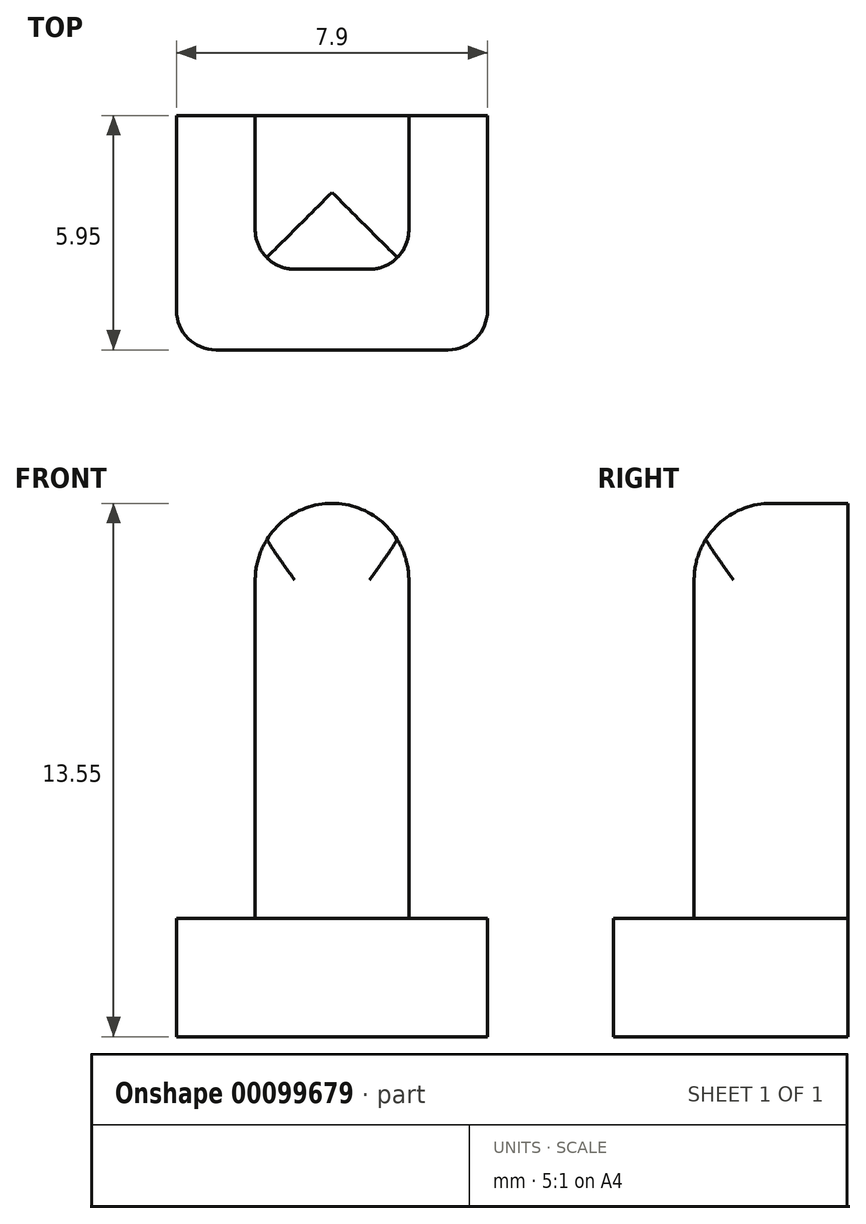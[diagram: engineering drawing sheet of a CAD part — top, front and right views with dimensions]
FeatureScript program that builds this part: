
annotation { "Feature Type Name" : "Feature", "Feature Type Description" : "" }
export const myFeature = defineFeature(function(context is Context, id is Id, definition is map)
    precondition{}
    {
        {
            var Q0;
            Q0=qCreatedBy(makeId("Top.planeOp"),FACE);
            var sketch = newSketch(context, id + "F0", { "sketchPlane" : qUnion([Q0])});
            skLineSegment(sketch, "E0.bottom", {"start": v(-3.95, 0) * mm, "end": v(3.95, 0) * mm});
            skLineSegment(sketch, "E0.top", {"start": v(-3.95, -5.95) * mm, "end": v(3.95, -5.95) * mm});
            skLineSegment(sketch, "E0.left", {"start": v(-3.95, 0) * mm, "end": v(-3.95, -5.95) * mm});
            skLineSegment(sketch, "E0.right", {"start": v(3.95, 0) * mm, "end": v(3.95, -5.95) * mm});
            skSolve(sketch);
        }
        {
            var Q0;
            Q0=makeQuery(id+"F0.imprint","IMPRINT",FACE,{"disambiguationData":[TD([[makeQuery(id+"F0.imprint","IMPRINT",EDGE,{"derivedFrom":sQuery(id+"F0.wireOp",EDGE,"E0.bottom")}),-1.0]])]});
            extrude(context, id + "F1", {"entities" : qUnion([Q0]), "depth" : 3 * mm});
        }
        {
            var Q0;
            Q0=makeQuery(id+"F1.opExtrude","CAP_FACE",FACE,{"disambiguationData":[OSD([sQuery(id+"F0.wireOp",EDGE,"E0.bottom"),sQuery(id+"F0.wireOp",EDGE,"E0.top"),sQuery(id+"F0.wireOp",EDGE,"E0.left"),sQuery(id+"F0.wireOp",EDGE,"E0.right")])],"isStart":false});
            var sketch = newSketch(context, id + "F2", { "sketchPlane" : qUnion([Q0])});
            skLineSegment(sketch, "E1.bottom", {"start": v(-1.95, 0) * mm, "end": v(1.95, 0) * mm});
            skLineSegment(sketch, "E1.top", {"start": v(-1.95, -3.9) * mm, "end": v(1.95, -3.9) * mm});
            skLineSegment(sketch, "E1.left", {"start": v(-1.95, 0) * mm, "end": v(-1.95, -3.9) * mm});
            skLineSegment(sketch, "E1.right", {"start": v(1.95, 0) * mm, "end": v(1.95, -3.9) * mm});
            skSolve(sketch);
        }
        {
            var Q0;
            Q0 = qSketchRegion(id + "F2", true);
            extrude(context, id + "F3", {"entities" : qUnion([Q0]), "operationType" : NewBodyOperationType.ADD, "depth" : 10.55 * mm});
        }
        {
            var Q0;
            Q0=makeQuery(id+"F3.opExtrude","CAP_EDGE",EDGE,{"disambiguationData":[OSD([sQuery(id+"F2.wireOp",EDGE,"E1.top")])],"isStart":false});
            var Q1;
            Q1=makeQuery(id+"F3.opExtrude","CAP_EDGE",EDGE,{"disambiguationData":[OSD([sQuery(id+"F2.wireOp",EDGE,"E1.left")])],"isStart":false});
            var Q2;
            Q2=makeQuery(id+"F3.opExtrude","CAP_EDGE",EDGE,{"disambiguationData":[OSD([sQuery(id+"F2.wireOp",EDGE,"E1.right")])],"isStart":false});
            fillet(context, id + "F4", {"entities" : qUnion([Q0, Q1, Q2]), "radius" : 1.95 * mm, "allowEdgeOverflow" : false});
        }
        {
            var Q0;
            Q0=makeQuery(id+"F1.opExtrude","SWEPT_EDGE",EDGE,{"disambiguationData":[OSD([sQuery(id+"F0.wireOp",EDGE,"E0.top"),sQuery(id+"F0.wireOp",EDGE,"E0.left")])]});
            var Q1;
            Q1=makeQuery(id+"F1.opExtrude","SWEPT_EDGE",EDGE,{"disambiguationData":[OSD([sQuery(id+"F0.wireOp",EDGE,"E0.top"),sQuery(id+"F0.wireOp",EDGE,"E0.right")])]});
            fillet(context, id + "F5", {"entities" : qUnion([Q0, Q1]), "radius" : 1 * mm, "allowEdgeOverflow" : false});
        }
        {
            var Q0;
            Q0=makeQuery(id+"F3.opExtrude","SWEPT_EDGE",EDGE,{"disambiguationData":[OSD([sQuery(id+"F2.wireOp",EDGE,"E1.top"),sQuery(id+"F2.wireOp",EDGE,"E1.right")])]});
            var Q1;
            Q1=makeQuery(id+"F3.opExtrude","SWEPT_EDGE",EDGE,{"disambiguationData":[OSD([sQuery(id+"F2.wireOp",EDGE,"E1.top"),sQuery(id+"F2.wireOp",EDGE,"E1.left")])]});
            fillet(context, id + "F6", {"entities" : qUnion([Q0, Q1]), "radius" : 1 * mm, "allowEdgeOverflow" : false});
        }
    });
